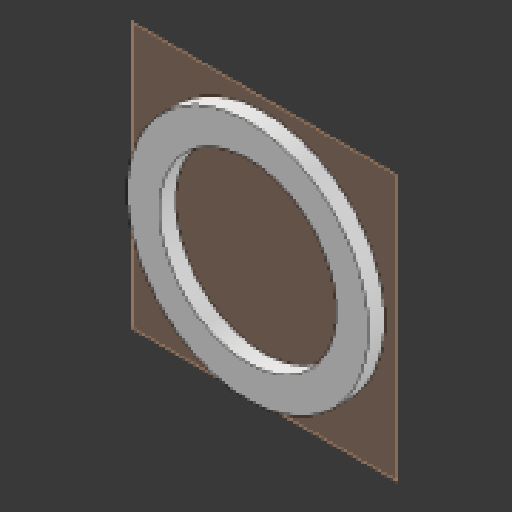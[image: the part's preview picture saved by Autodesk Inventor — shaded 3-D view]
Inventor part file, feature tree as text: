
AUTODESK INVENTOR PART (.ipt)
format: ipt  version: 2023 (Build 270158000, 158)  size: 91,648 bytes
history: native  units: mm
features: other x3, plane x1, extrude x1, sketch x1, reference x1
ambient origin geometry x8: Origin, YZ Plane, XZ Plane, XY Plane, X Axis, Y Axis, Z Axis, Center Point
bodies: Solid1 (feature_tree)
feature tree (7):
  plane  "Work Plane1"
  extrude  "Extrusion1"  Depth=4.0mm
  sketch  "Sketch1"  dims[d0=60.0mm d1=8.0mm d2=4.0mm d3=0.0mm]
  reference  "Reference1"
  other  "<userpath>\Desktop\NEARLab\dVRK\Trocar_Entry_Membrane\Assembly.iam"
  other  "Assembly.iam"
  other  "Membrane:1"
